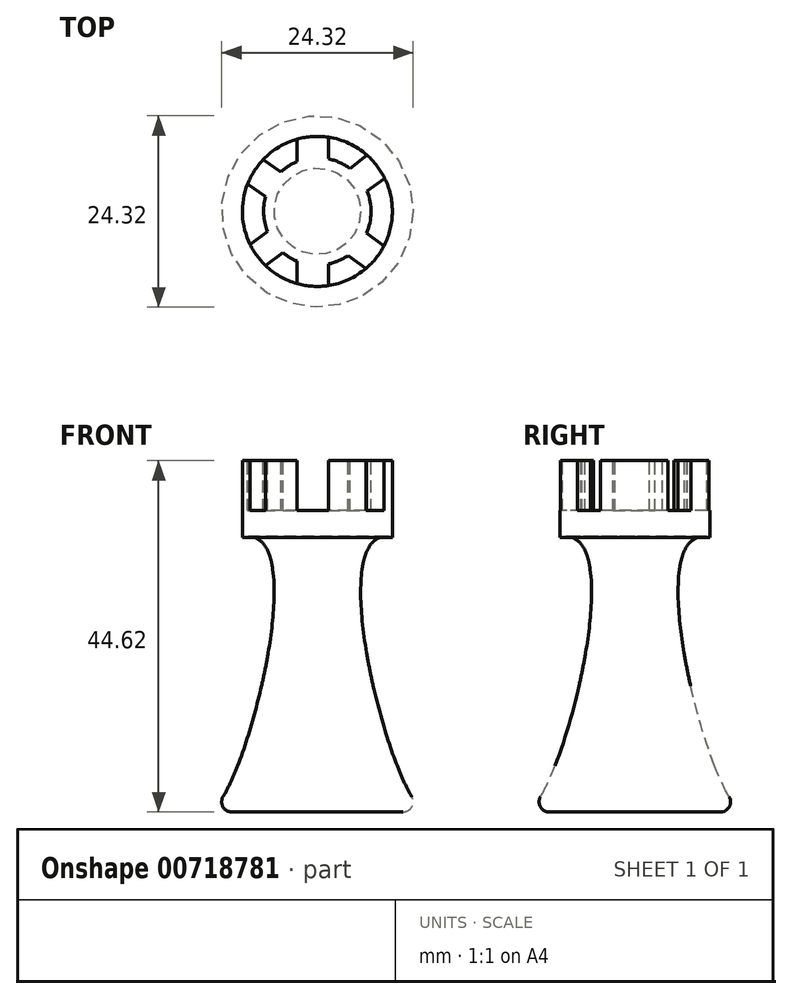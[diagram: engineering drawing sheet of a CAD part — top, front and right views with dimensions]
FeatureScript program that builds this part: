
annotation { "Feature Type Name" : "Feature", "Feature Type Description" : "" }
export const myFeature = defineFeature(function(context is Context, id is Id, definition is map)
    precondition{}
    {
        {
            var Q0;
            Q0=qCreatedBy(makeId("Front.planeOp"),FACE);
            var sketch = newSketch(context, id + "F0", { "sketchPlane" : qUnion([Q0])});
            skLineSegment(sketch, "E0", {"start": v(-30.77, -9.26) * mm, "end": v(-2.83, -9.26) * mm});
            skLineSegment(sketch, "E1", {"start": v(-16.8, -9.26) * mm, "end": v(-16.8, 64.84) * mm, "construction": true});
            skFitSpline(sketch, "E2", {"points": [v(-7.28, 25.63) * mm, v(-2.83, -9.26) * mm], "startDerivative": vector(-28.58, 6.48) * mm, "endDerivative": vector(12.53, 0) * mm});
            skLineSegment(sketch, "E3", {"start": v(-7.28, 25.63) * mm, "end": v(-7.28, 35.36) * mm});
            skLineSegment(sketch, "E4", {"start": v(-7.28, 35.36) * mm, "end": v(-16.8, 35.36) * mm});
            skLineSegment(sketch, "E5.MirrorCS", {"start": v(-26.33, 35.36) * mm, "end": v(-16.8, 35.36) * mm});
            skLineSegment(sketch, "E6.MirrorCS", {"start": v(-26.33, 25.63) * mm, "end": v(-26.33, 35.36) * mm});
            skFitSpline(sketch, "E7.MirrorCS", {"points": [v(-26.33, 25.63) * mm, v(-30.77, -9.26) * mm], "startDerivative": vector(28.58, 6.48) * mm, "endDerivative": vector(-12.53, 0) * mm});
            skLineSegment(sketch, "E8", {"start": v(-16.8, 35.36) * mm, "end": v(-16.8, -9.26) * mm});
            skFitSpline(sketch, "E9", {"points": [v(-28.5, -6.84) * mm, v(-30.77, -5.36) * mm, v(-26.94, -3.43) * mm], "startDerivative": vector(-6.45, 4.71) * mm, "endDerivative": vector(9.16, 2.46) * mm});
            skFitSpline(sketch, "E10", {"points": [v(-23.89, 6.74) * mm, v(-26.73, 9.44) * mm, v(-23.57, 11.34) * mm, v(-23.06, 10.9) * mm], "startDerivative": vector(-13.8, 6.75) * mm, "endDerivative": vector(3.73, -3.95) * mm});
            skFitSpline(sketch, "E11", {"points": [v(-23.16, 24.02) * mm, v(-24.83, 22.72) * mm, v(-22.47, 21.54) * mm], "startDerivative": vector(-5.92, -3.08) * mm, "endDerivative": vector(7.28, -1.97) * mm});
            skSolve(sketch);
        }
        {
            var Q0;
            Q0=makeQuery(id+"F0.imprint","IMPRINT",FACE,{"disambiguationData":[TD([[makeQuery(id+"F0.imprint","IMPRINT",EDGE,{"derivedFrom":sQuery(id+"F0.wireOp",EDGE,"E5.MirrorCS")}),-1.0]])]});
            var Q1;
            Q1=sQuery(id+"F0.wireOp",EDGE,"E8");
            revolve(context, id + "F1", {"surfaceOperationType" : NewSurfaceOperationType.NEW, "entities" : qUnion([Q0]), "axis" : qUnion([Q1]), "revolveType" : RevolveType.FULL});
        }
        {
            var Q0;
            Q0=makeQuery(id+"F1.opRevolve","SWEPT_EDGE",EDGE,{"disambiguationData":[OSD([sQuery(id+"F0.wireOp",EDGE,"E0"),sQuery(id+"F0.wireOp",EDGE,"E7.MirrorCS")])]});
            fillet(context, id + "F2", {"entities" : qUnion([Q0]), "radius" : 1.27 * mm, "tangentPropagation" : true, "allowEdgeOverflow" : false});
        }
        {
            var Q0;
            Q0=makeQuery(id+"F1.opRevolve","SWEPT_FACE",FACE,{"disambiguationData":[OSD([sQuery(id+"F0.wireOp",EDGE,"E5.MirrorCS")])]});
            var sketch = newSketch(context, id + "F3", { "sketchPlane" : qUnion([Q0])});
            skLineSegment(sketch, "E12", {"start": v(-19.37, 9.17) * mm, "end": v(-19.37, 6.32) * mm});
            skLineSegment(sketch, "E13.MirrorCS", {"start": v(-15.41, 9.44) * mm, "end": v(-15.41, 6.68) * mm});
            skLineSegment(sketch, "E14", {"start": v(-25.66, 3.5) * mm, "end": v(-23.37, 1.85) * mm});
            skLineSegment(sketch, "E15.MirrorCS", {"start": v(-23.69, 6.6) * mm, "end": v(-21.45, 5) * mm});
            skLineSegment(sketch, "E16", {"start": v(-10.48, 7.13) * mm, "end": v(-12.69, 5.45) * mm});
            skLineSegment(sketch, "E17.MirrorCS", {"start": v(-8.18, 4.25) * mm, "end": v(-10.48, 2.57) * mm});
            skLineSegment(sketch, "E18.trimOffspring", {"start": v(-21.18, -5.23) * mm, "end": v(-23.48, -6.9) * mm});
            skLineSegment(sketch, "E19.trimOffspring", {"start": v(-10.57, -2.78) * mm, "end": v(-8.33, -4.38) * mm});
            skLineSegment(sketch, "E20.trimOffspring", {"start": v(-15.41, -6.68) * mm, "end": v(-15.41, -9.44) * mm});
            skLineSegment(sketch, "E21.trimOffspring", {"start": v(-23.14, -2.54) * mm, "end": v(-25.34, -4.22) * mm});
            skLineSegment(sketch, "E22.trimOffspring", {"start": v(-19.37, -6.32) * mm, "end": v(-19.37, -9.17) * mm});
            skLineSegment(sketch, "E23.trimOffspring", {"start": v(-12.92, -5.62) * mm, "end": v(-10.63, -7.26) * mm});
            skArc(sketch, "E24", {"start": v(-19.37, 6.32) * mm, "mid": v(-20.47, 5.76) * mm, "end": v(-21.45, 5) * mm});
            skArc(sketch, "E25.trimOffspring", {"start": v(-23.37, 1.85) * mm, "mid": v(-23.62, -0.36) * mm, "end": v(-23.14, -2.54) * mm});
            skArc(sketch, "E26.trimOffspring", {"start": v(-12.69, 5.45) * mm, "mid": v(-13.98, 6.22) * mm, "end": v(-15.41, 6.68) * mm});
            skArc(sketch, "E27.trimOffspring", {"start": v(-10.57, -2.78) * mm, "mid": v(-9.97, -0.11) * mm, "end": v(-10.48, 2.57) * mm});
            skArc(sketch, "E28.trimOffspring", {"start": v(-15.41, -6.68) * mm, "mid": v(-14.11, -6.28) * mm, "end": v(-12.92, -5.62) * mm});
            skArc(sketch, "E29.trimOffspring", {"start": v(-21.18, -5.23) * mm, "mid": v(-20.32, -5.85) * mm, "end": v(-19.37, -6.32) * mm});
            skSolve(sketch);
        }
        {
            var Q0;
            {var subQ0=sQuery(id+"F3.wireOp",EDGE,"E12");Q0=makeQuery(id+"F3.imprint","IMPRINT",FACE,{"disambiguationData":[TD([[makeQuery(id+"F3.imprint","IMPRINT",EDGE,{"derivedFrom":subQ0}),1.0]])]});}
            extrude(context, id + "F4", {"entities" : qUnion([Q0]), "operationType" : NewBodyOperationType.REMOVE, "oppositeDirection" : true, "depth" : 6.35 * mm, "offsetDistance" : 25.4 * mm});
        }
    });
